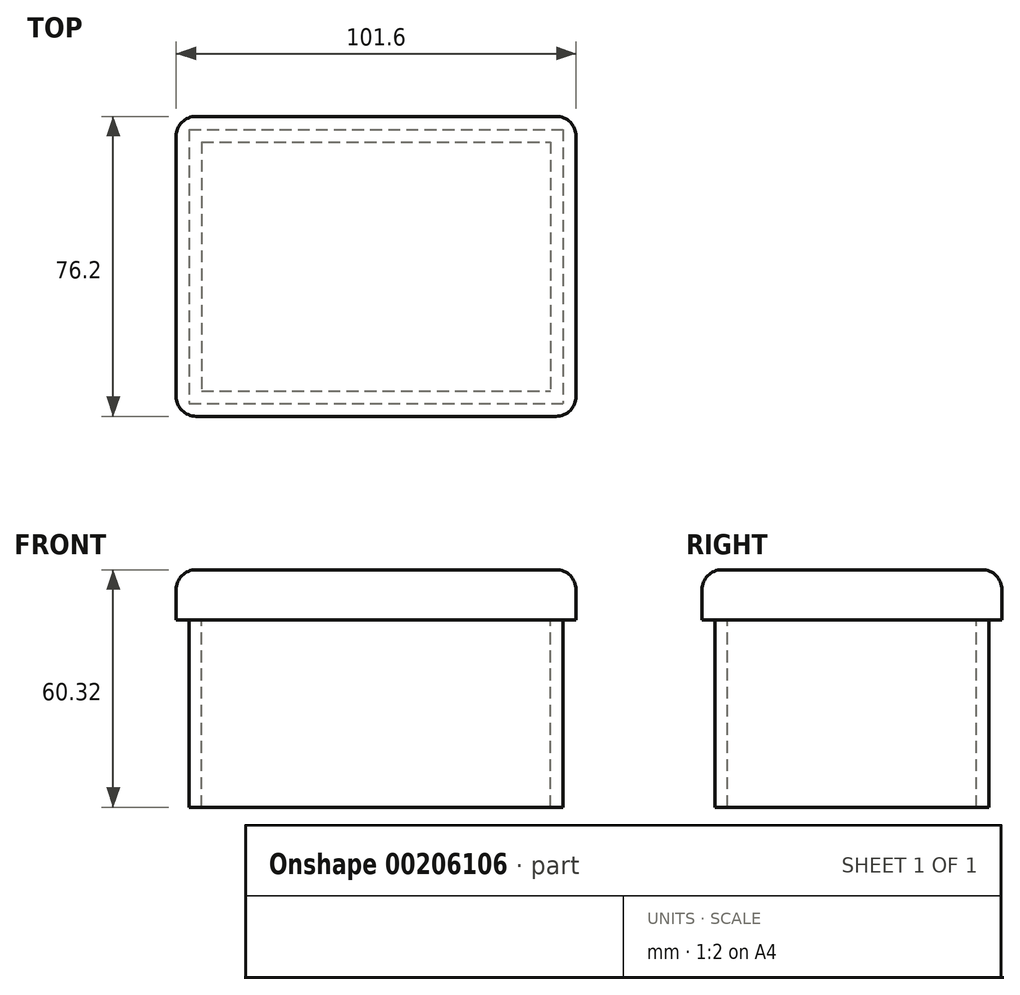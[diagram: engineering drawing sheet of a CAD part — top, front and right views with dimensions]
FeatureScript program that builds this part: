
annotation { "Feature Type Name" : "Feature", "Feature Type Description" : "" }
export const myFeature = defineFeature(function(context is Context, id is Id, definition is map)
    precondition{}
    {
        {
            var Q0;
            Q0=qCreatedBy(makeId("Top.planeOp"),FACE);
            var sketch = newSketch(context, id + "F0", { "sketchPlane" : qUnion([Q0])});
            skLineSegment(sketch, "E0.bottom", {"start": v(-50.8, 38.1) * mm, "end": v(50.8, 38.1) * mm});
            skLineSegment(sketch, "E0.top", {"start": v(-50.8, -38.1) * mm, "end": v(50.8, -38.1) * mm});
            skLineSegment(sketch, "E0.left", {"start": v(-50.8, 38.1) * mm, "end": v(-50.8, -38.1) * mm});
            skLineSegment(sketch, "E0.right", {"start": v(50.8, 38.1) * mm, "end": v(50.8, -38.1) * mm});
            skPoint(sketch, "E0.middle", {"position": v(0, 0) * mm});
            skSolve(sketch);
        }
        {
            var Q0;
            Q0=makeQuery(id+"F0.imprint","IMPRINT",FACE,{"disambiguationData":[TD([[makeQuery(id+"F0.imprint","IMPRINT",EDGE,{"derivedFrom":sQuery(id+"F0.wireOp",EDGE,"E0.bottom")}),-1.0]])]});
            extrude(context, id + "F1", {"entities" : qUnion([Q0]), "depth" : 12.7 * mm});
        }
        {
            var Q0;
            Q0=makeQuery(id+"F1.opExtrude","CAP_EDGE",EDGE,{"disambiguationData":[OSD([sQuery(id+"F0.wireOp",EDGE,"E0.top")])],"isStart":false});
            var Q1;
            Q1=makeQuery(id+"F1.opExtrude","CAP_EDGE",EDGE,{"disambiguationData":[OSD([sQuery(id+"F0.wireOp",EDGE,"E0.left")])],"isStart":false});
            var Q2;
            Q2=makeQuery(id+"F1.opExtrude","CAP_EDGE",EDGE,{"disambiguationData":[OSD([sQuery(id+"F0.wireOp",EDGE,"E0.bottom")])],"isStart":false});
            var Q3;
            Q3=makeQuery(id+"F1.opExtrude","CAP_EDGE",EDGE,{"disambiguationData":[OSD([sQuery(id+"F0.wireOp",EDGE,"E0.right")])],"isStart":false});
            var Q4;
            Q4=makeQuery(id+"F1.opExtrude","SWEPT_EDGE",EDGE,{"disambiguationData":[OSD([sQuery(id+"F0.wireOp",EDGE,"E0.top"),sQuery(id+"F0.wireOp",EDGE,"E0.right")])]});
            var Q5;
            Q5=makeQuery(id+"F1.opExtrude","SWEPT_EDGE",EDGE,{"disambiguationData":[OSD([sQuery(id+"F0.wireOp",EDGE,"E0.bottom"),sQuery(id+"F0.wireOp",EDGE,"E0.right")])]});
            var Q6;
            Q6=makeQuery(id+"F1.opExtrude","SWEPT_EDGE",EDGE,{"disambiguationData":[OSD([sQuery(id+"F0.wireOp",EDGE,"E0.bottom"),sQuery(id+"F0.wireOp",EDGE,"E0.left")])]});
            var Q7;
            Q7=makeQuery(id+"F1.opExtrude","SWEPT_EDGE",EDGE,{"disambiguationData":[OSD([sQuery(id+"F0.wireOp",EDGE,"E0.top"),sQuery(id+"F0.wireOp",EDGE,"E0.left")])]});
            fillet(context, id + "F2", {"entities" : qUnion([Q0, Q1, Q2, Q3, Q4, Q5, Q6, Q7]), "radius" : 5.08 * mm, "tangentPropagation" : true, "allowEdgeOverflow" : false});
        }
        {
            var Q0;
            Q0=makeQuery(id+"F1.opExtrude","CAP_FACE",FACE,{"disambiguationData":[OSD([sQuery(id+"F0.wireOp",EDGE,"E0.bottom"),sQuery(id+"F0.wireOp",EDGE,"E0.top"),sQuery(id+"F0.wireOp",EDGE,"E0.left"),sQuery(id+"F0.wireOp",EDGE,"E0.right")])],"isStart":true});
            var sketch = newSketch(context, id + "F3", { "sketchPlane" : qUnion([Q0])});
            skLineSegment(sketch, "E1.0", {"start": v(-47.5, 34.8) * mm, "end": v(47.5, 34.8) * mm});
            skLineSegment(sketch, "E1.1", {"start": v(-47.5, -34.8) * mm, "end": v(-47.5, 34.8) * mm});
            skLineSegment(sketch, "E1.2", {"start": v(-47.5, -34.8) * mm, "end": v(47.5, -34.8) * mm});
            skLineSegment(sketch, "E1.3", {"start": v(47.5, -34.8) * mm, "end": v(47.5, 34.8) * mm});
            skLineSegment(sketch, "E2.0", {"start": v(-44.32, 31.62) * mm, "end": v(44.32, 31.62) * mm});
            skLineSegment(sketch, "E2.1", {"start": v(-44.32, -31.62) * mm, "end": v(-44.32, 31.62) * mm});
            skLineSegment(sketch, "E2.2", {"start": v(-44.32, -31.62) * mm, "end": v(44.32, -31.62) * mm});
            skLineSegment(sketch, "E2.3", {"start": v(44.32, -31.62) * mm, "end": v(44.32, 31.62) * mm});
            skSolve(sketch);
        }
        {
            var Q0;
            Q0=makeQuery(id+"F3.imprint","IMPRINT",FACE,{"disambiguationData":[TD([[makeQuery(id+"F3.imprint","IMPRINT",EDGE,{"derivedFrom":sQuery(id+"F3.wireOp",EDGE,"E1.0")}),-1.0]])]});
            extrude(context, id + "F4", {"entities" : qUnion([Q0]), "operationType" : NewBodyOperationType.ADD, "depth" : 47.62 * mm});
        }
    });
